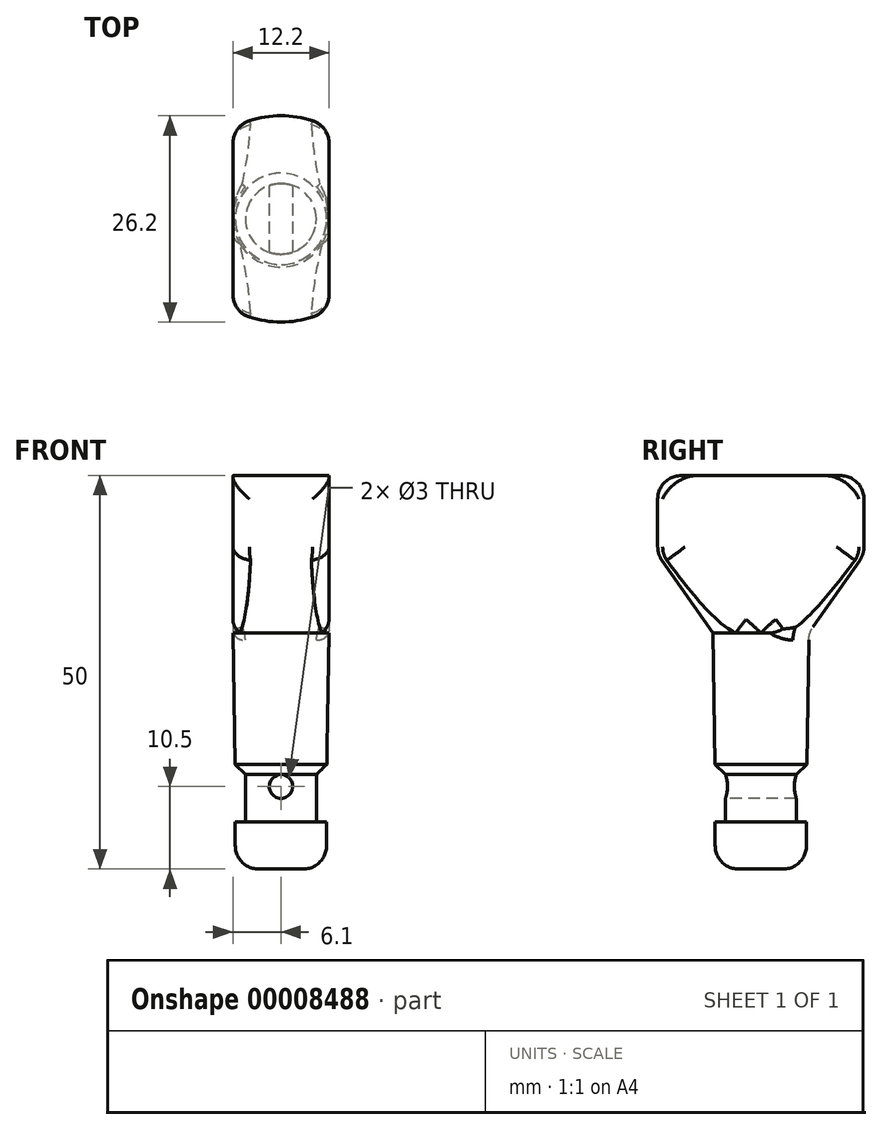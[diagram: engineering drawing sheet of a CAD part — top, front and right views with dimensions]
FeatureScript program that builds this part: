
annotation { "Feature Type Name" : "Feature", "Feature Type Description" : "" }
export const myFeature = defineFeature(function(context is Context, id is Id, definition is map)
    precondition{}
    {
        {
            var Q0;
            Q0=qCreatedBy(makeId("Front.planeOp"),FACE);
            var sketch = newSketch(context, id + "F0", { "sketchPlane" : qUnion([Q0])});
            skLineSegment(sketch, "E0.rect.bottom", {"start": v(-6.1, 30) * mm, "end": v(0, 30) * mm});
            skLineSegment(sketch, "E0.rect.top", {"start": v(-5.8, 0) * mm, "end": v(0, 0) * mm});
            skLineSegment(sketch, "E0.rect.left", {"start": v(-6.1, 30) * mm, "end": v(-5.82, 13.32) * mm});
            skPoint(sketch, "E0.rect.middle", {"position": v(0, 0) * mm});
            skLineSegment(sketch, "E1", {"start": v(0, 30) * mm, "end": v(0, 12) * mm});
            skLineSegment(sketch, "E2", {"start": v(-5.8, 6) * mm, "end": v(0, 6) * mm});
            skLineSegment(sketch, "E3", {"start": v(-4.5, 12) * mm, "end": v(0, 12) * mm});
            skLineSegment(sketch, "E4", {"start": v(-4.5, 12) * mm, "end": v(-4.5, 6) * mm});
            skLineSegment(sketch, "E5.trimOffspring", {"start": v(-5.8, 6) * mm, "end": v(-5.8, 0) * mm});
            skLineSegment(sketch, "E6", {"start": v(0, 12) * mm, "end": v(0, 6) * mm});
            skLineSegment(sketch, "E7", {"start": v(0, 6) * mm, "end": v(0, 0) * mm});
            skCircle(sketch, "E8", {"center": v(0, 10.5) * mm, "radius": 1.5 * mm});
            skLineSegment(sketch, "E9", {"start": v(-6.1, 30) * mm, "end": v(-13.1, 40) * mm});
            skLineSegment(sketch, "E10", {"start": v(-13.1, 40) * mm, "end": v(-13.1, 50) * mm});
            skLineSegment(sketch, "E11", {"start": v(-13.1, 50) * mm, "end": v(0, 50) * mm});
            skLineSegment(sketch, "E12", {"start": v(0, 50) * mm, "end": v(0, 30) * mm});
            skLineSegment(sketch, "E13", {"start": v(-6.1, 50) * mm, "end": v(-6.1, 30) * mm});
            skLineSegment(sketch, "E14.0.MirrorCS", {"start": v(6.1, 50) * mm, "end": v(6.1, 30) * mm});
            skLineSegment(sketch, "E15.0.MirrorCS", {"start": v(13.1, 50) * mm, "end": v(0, 50) * mm});
            skLineSegment(sketch, "E16.0.MirrorCS", {"start": v(13.1, 40) * mm, "end": v(13.1, 50) * mm});
            skLineSegment(sketch, "E17.0.MirrorCS", {"start": v(6.1, 30) * mm, "end": v(13.1, 40) * mm});
            skLineSegment(sketch, "E18.0.MirrorCS", {"start": v(6.1, 30) * mm, "end": v(0, 30) * mm});
            skLineSegment(sketch, "E19", {"start": v(-4.5, 12) * mm, "end": v(-5.82, 13.32) * mm});
            skPoint(sketch, "E20.orphan", {"position": v(-5.8, 12) * mm});
            skSolve(sketch);
        }
        {
            var Q0;
            Q0=makeQuery(id+"F0.imprint","IMPRINT",FACE,{"disambiguationData":[TD([[makeQuery(id+"F0.imprint","IMPRINT",EDGE,{"derivedFrom":sQuery(id+"F0.wireOp",EDGE,"E0.rect.top")}),1.0]])]});
            var Q1;
            {var subQ8=sQuery(id+"F0.wireOp",EDGE,"E4");Q1=makeQuery(id+"F0.imprint","IMPRINT",FACE,{"disambiguationData":[TD([[makeQuery(id+"F0.imprint","IMPRINT",EDGE,{"derivedFrom":subQ8}),1.0]])]});}
            var Q2;
            Q2=makeQuery(id+"F0.imprint","IMPRINT",FACE,{"disambiguationData":[TD([[makeQuery(id+"F0.imprint","IMPRINT",EDGE,{"derivedFrom":sQuery(id+"F0.wireOp",EDGE,"E0.rect.bottom")}),-1.0]])]});
            var Q3;
            Q3=makeQuery(id+"F0.imprint","IMPRINT",FACE,{"disambiguationData":[TD([[makeQuery(id+"F0.imprint","IMPRINT",EDGE,{"derivedFrom":sQuery(id+"F0.wireOp",EDGE,"E0.rect.bottom")}),1.0]])]});
            var Q4;
            {var subQ0=sQuery(id+"F0.wireOp",EDGE,"E8");var subQ1=sQuery(id+"F0.wireOp",EDGE,"E6");var subQ3=makeQuery(id+"F0.imprint","INTERSECT",VERTEX,{"disambiguationData":[OD(0.0)],"derivedFrom":[subQ1,subQ0]});Q4=makeQuery(id+"F0.imprint","IMPRINT",FACE,{"disambiguationData":[TD([[makeQuery(id+"F0.imprint","IMPRINT",EDGE,{"disambiguationData":[TD([[subQ3,-1.0]])],"derivedFrom":subQ1}),-1.0]])]});}
            var Q5;
            {var subQ3=sQuery(id+"F0.wireOp",EDGE,"E9");Q5=makeQuery(id+"F0.imprint","IMPRINT",FACE,{"disambiguationData":[TD([[makeQuery(id+"F0.imprint","IMPRINT",EDGE,{"derivedFrom":subQ3}),-1.0]])]});}
            var Q6;
            Q6=sQuery(id+"F0.wireOp",EDGE,"E1");
            revolve(context, id + "F1", {"entities" : qUnion([Q0, Q1, Q2, Q3, Q4, Q5]), "axis" : qUnion([Q6]), "revolveType" : RevolveType.FULL});
        }
        {
            var Q0;
            {var subQ0=sQuery(id+"F0.wireOp",EDGE,"E8");var subQ1=sQuery(id+"F0.wireOp",EDGE,"E6");var subQ2=makeQuery(id+"F0.imprint","INTERSECT",VERTEX,{"derivedFrom":[subQ1,subQ0]});Q0=makeQuery(id+"F0.imprint","IMPRINT",FACE,{"disambiguationData":[TD([[makeQuery(id+"F0.imprint","IMPRINT",EDGE,{"disambiguationData":[TD([[subQ2,1.0]])],"derivedFrom":subQ1}),-1.0]])]});}
            var Q1;
            {var subQ0=sQuery(id+"F0.wireOp",EDGE,"E8");var subQ1=sQuery(id+"F0.wireOp",EDGE,"E6");var subQ2=makeQuery(id+"F0.imprint","INTERSECT",VERTEX,{"derivedFrom":[subQ1,subQ0]});Q1=makeQuery(id+"F0.imprint","IMPRINT",FACE,{"disambiguationData":[TD([[makeQuery(id+"F0.imprint","IMPRINT",EDGE,{"disambiguationData":[TD([[subQ2,1.0]])],"derivedFrom":subQ1}),1.0]])]});}
            extrude(context, id + "F2", {"entities" : qUnion([Q0, Q1]), "operationType" : NewBodyOperationType.REMOVE, "endBound" : BoundingType.SYMMETRIC, "oppositeDirection" : true, "depth" : 25 * mm});
        }
        {
            var Q0;
            Q0=makeQuery(id+"F1.opRevolve","SWEPT_EDGE",EDGE,{"disambiguationData":[OSD([sQuery(id+"F0.wireOp",EDGE,"E0.rect.top"),sQuery(id+"F0.wireOp",EDGE,"E5.trimOffspring")])]});
            fillet(context, id + "F3", {"entities" : qUnion([Q0]), "radius" : 3 * mm, "tangentPropagation" : true, "allowEdgeOverflow" : false});
        }
        {
            var Q0;
            {var subQ3=sQuery(id+"F0.wireOp",EDGE,"E9");Q0=makeQuery(id+"F0.imprint","IMPRINT",FACE,{"disambiguationData":[TD([[makeQuery(id+"F0.imprint","IMPRINT",EDGE,{"derivedFrom":subQ3}),-1.0]])]});}
            var Q1;
            {var subQ2=sQuery(id+"F0.wireOp",EDGE,"E14.0.MirrorCS");Q1=makeQuery(id+"F0.imprint","IMPRINT",FACE,{"disambiguationData":[TD([[makeQuery(id+"F0.imprint","IMPRINT",EDGE,{"derivedFrom":subQ2}),1.0]])]});}
            extrude(context, id + "F4", {"entities" : qUnion([Q0, Q1]), "operationType" : NewBodyOperationType.REMOVE, "endBound" : BoundingType.SYMMETRIC, "oppositeDirection" : true, "depth" : 25 * mm});
        }
        {
            var Q0;
            Q0=makeQuery(id+"F4.boolean.opBoolean","SPLIT",EDGE,{"disambiguationData":[OD(0.0)],"derivedFrom":makeQuery(id+"F1.opRevolve","SWEPT_EDGE",EDGE,{"disambiguationData":[OSD([sQuery(id+"F0.wireOp",EDGE,"E10"),sQuery(id+"F0.wireOp",EDGE,"E11")])]})});
            var Q1;
            Q1=makeQuery(id+"F4.boolean.opBoolean","COPY",EDGE,{"derivedFrom":makeQuery(id+"F4.opExtrude","SWEPT_EDGE",EDGE,{"disambiguationData":[OSD([sQuery(id+"F0.wireOp",EDGE,"E14.0.MirrorCS"),sQuery(id+"F0.wireOp",EDGE,"E15.0.MirrorCS")])]})});
            var Q2;
            Q2=makeQuery(id+"F4.boolean.opBoolean","SPLIT",EDGE,{"disambiguationData":[OD(1.0)],"derivedFrom":makeQuery(id+"F1.opRevolve","SWEPT_EDGE",EDGE,{"disambiguationData":[OSD([sQuery(id+"F0.wireOp",EDGE,"E10"),sQuery(id+"F0.wireOp",EDGE,"E11")])]})});
            var Q3;
            Q3=makeQuery(id+"F4.boolean.opBoolean","COPY",EDGE,{"derivedFrom":makeQuery(id+"F4.opExtrude","SWEPT_EDGE",EDGE,{"disambiguationData":[OSD([sQuery(id+"F0.wireOp",EDGE,"E11"),sQuery(id+"F0.wireOp",EDGE,"E13")])]})});
            var Q4;
            Q4=makeQuery(id+"F4.boolean.opBoolean","INTERSECT",EDGE,{"disambiguationData":[OD(0.0)],"derivedFrom":[makeQuery(id+"F1.opRevolve","SWEPT_FACE",FACE,{"disambiguationData":[OSD([sQuery(id+"F0.wireOp",EDGE,"E10")])]}),makeQuery(id+"F4.opExtrude","SWEPT_FACE",FACE,{"disambiguationData":[OSD([sQuery(id+"F0.wireOp",EDGE,"E14.0.MirrorCS")])]})]});
            var Q5;
            Q5=makeQuery(id+"F4.boolean.opBoolean","INTERSECT",EDGE,{"disambiguationData":[OD(1.0)],"derivedFrom":[makeQuery(id+"F1.opRevolve","SWEPT_FACE",FACE,{"disambiguationData":[OSD([sQuery(id+"F0.wireOp",EDGE,"E10")])]}),makeQuery(id+"F4.opExtrude","SWEPT_FACE",FACE,{"disambiguationData":[OSD([sQuery(id+"F0.wireOp",EDGE,"E14.0.MirrorCS")])]})]});
            var Q6;
            Q6=makeQuery(id+"F4.boolean.opBoolean","INTERSECT",EDGE,{"disambiguationData":[OD(1.0)],"derivedFrom":[makeQuery(id+"F1.opRevolve","SWEPT_FACE",FACE,{"disambiguationData":[OSD([sQuery(id+"F0.wireOp",EDGE,"E10")])]}),makeQuery(id+"F4.opExtrude","SWEPT_FACE",FACE,{"disambiguationData":[OSD([sQuery(id+"F0.wireOp",EDGE,"E13")])]})]});
            var Q7;
            Q7=makeQuery(id+"F4.boolean.opBoolean","INTERSECT",EDGE,{"disambiguationData":[OD(0.0)],"derivedFrom":[makeQuery(id+"F1.opRevolve","SWEPT_FACE",FACE,{"disambiguationData":[OSD([sQuery(id+"F0.wireOp",EDGE,"E10")])]}),makeQuery(id+"F4.opExtrude","SWEPT_FACE",FACE,{"disambiguationData":[OSD([sQuery(id+"F0.wireOp",EDGE,"E13")])]})]});
            var Q8;
            Q8=makeQuery(id+"F4.boolean.opBoolean","SPLIT",EDGE,{"disambiguationData":[OD(0.0)],"derivedFrom":makeQuery(id+"F1.opRevolve","SWEPT_EDGE",EDGE,{"disambiguationData":[OSD([sQuery(id+"F0.wireOp",EDGE,"E9"),sQuery(id+"F0.wireOp",EDGE,"E10")])]})});
            var Q9;
            Q9=makeQuery(id+"F4.boolean.opBoolean","SPLIT",EDGE,{"disambiguationData":[OD(1.0)],"derivedFrom":makeQuery(id+"F1.opRevolve","SWEPT_EDGE",EDGE,{"disambiguationData":[OSD([sQuery(id+"F0.wireOp",EDGE,"E9"),sQuery(id+"F0.wireOp",EDGE,"E10")])]})});
            var Q10;
            Q10=makeQuery(id+"F4.boolean.opBoolean","INTERSECT",EDGE,{"disambiguationData":[OD(1.0)],"derivedFrom":[makeQuery(id+"F1.opRevolve","SWEPT_FACE",FACE,{"disambiguationData":[OSD([sQuery(id+"F0.wireOp",EDGE,"E9")])]}),makeQuery(id+"F4.opExtrude","SWEPT_FACE",FACE,{"disambiguationData":[OSD([sQuery(id+"F0.wireOp",EDGE,"E13")])]})]});
            var Q11;
            Q11=makeQuery(id+"F4.boolean.opBoolean","INTERSECT",EDGE,{"disambiguationData":[OD(0.0)],"derivedFrom":[makeQuery(id+"F1.opRevolve","SWEPT_FACE",FACE,{"disambiguationData":[OSD([sQuery(id+"F0.wireOp",EDGE,"E9")])]}),makeQuery(id+"F4.opExtrude","SWEPT_FACE",FACE,{"disambiguationData":[OSD([sQuery(id+"F0.wireOp",EDGE,"E14.0.MirrorCS")])]})]});
            fillet(context, id + "F5", {"entities" : qUnion([Q0, Q1, Q2, Q3, Q4, Q5, Q6, Q7, Q8, Q9, Q10, Q11]), "radius" : 3 * mm, "tangentPropagation" : true, "allowEdgeOverflow" : false});
        }
        {
            var Q0;
            Q0=makeQuery(id+"F4.boolean.opBoolean","SPLIT",EDGE,{"disambiguationData":[OD(1.0)],"derivedFrom":makeQuery(id+"F1.opRevolve","SWEPT_EDGE",EDGE,{"disambiguationData":[OSD([sQuery(id+"F0.wireOp",EDGE,"E0.rect.bottom"),sQuery(id+"F0.wireOp",EDGE,"E0.rect.left"),sQuery(id+"F0.wireOp",EDGE,"E9"),sQuery(id+"F0.wireOp",EDGE,"E13")])]})});
            fillet(context, id + "F6", {"entities" : qUnion([Q0]), "radius" : 3 * mm, "tangentPropagation" : true, "allowEdgeOverflow" : false});
        }
    });
